# Revit family: 11
name_source: partatom
category: Plumbing Fixtures
units: mm (PartAtom-declared; Revit-internal decimal feet)

## family parameters
Cut with Voids When Loaded = No
Host = Face
OmniClass Number = 23.45.05.21.11.11
OmniClass Title = Water Operated Water Closets
Part Type = Normal
Room Calculation Point = No
Round Connector Dimension = Use Diameter
Shared = Yes

## types (1)
- 3451528.020
    5901.100 Heavy duty open front less cover = No
    5905.100 Extra heavy duty open front less cover = No
    ADA Compliant = Yes
    Assembly Code = D2010110
    Bowl Shape = Elongated
    CW Connection = Yes
    CWFU = 5
    CalGreen Compliant = Yes
    Cold Water Connection Diameter = 1 1/2"
    Cold Water Connection Height = 11 1/2"
    Cold Water Connection Radius = 3/4"
    Cold Water Connection Width = 4 1/4"
    Cold Water Connection Width Constraint = 4 1/4"
    Default Elevation = 0"
    Description = Madera™ 15-Inch EverClean® Toilet System With Touchless Selectronic® Piston Flush Valve, 1.28 gpf/4.8 Lpf
    EPA WaterSense® Certified = Yes
    Finish = Vitreous China-American Standard-020-White
    Flow Rate = 25gpm (94.6 L/min.)
    Flush Rate = 1.28 gpf/4.8 Lpf
    Flush Valve Finish = Metal-American Standard-002-Polished Chrome
    Flush Valve to the Wall = 4"
    HW Connection = No
    HWFU = 0
    Height = 31 1/2"
    IAPMO Compliance = Fixture Compliance Certifications - Meets or Exceeds the Following Specifications: ASME A112.19.2-2008 / CSA B45.1-08 for Vitreous China Fixtures  Valve Compliance • ASSE 1037 • ANSI/ASME A112.19.2
    Installation Type = Floor Mounted
    Length = 14"
    Manufacturer = American Standard
    Material = Vitreous China-American Standard-020-White
    Model = 3451528.020
    Operating Pressure = 25 psi (flowing) - 80 psi (static)
    Price = Prices may vary. Please consult Manufacturer Representative for most up-to-date price list.
    Product Documentation Link = https://americanstandard.box.com
    Product Page URL = https://www.americanstandard-us.com
    Revised Date = 09/19/2022
    URL = https://www.americanstandard-us.com
    Vent Connection = No
    WFU = 5
    Waste Connection = Yes
    Waste Connection Diameter = 2 1/8"
    Waste Connection Radius = 1 1/16"
    Width = 28 1/4"

## geometry (parser evidence)
native form markers: Sweep x5
no freeform markers — native parametric forms only
